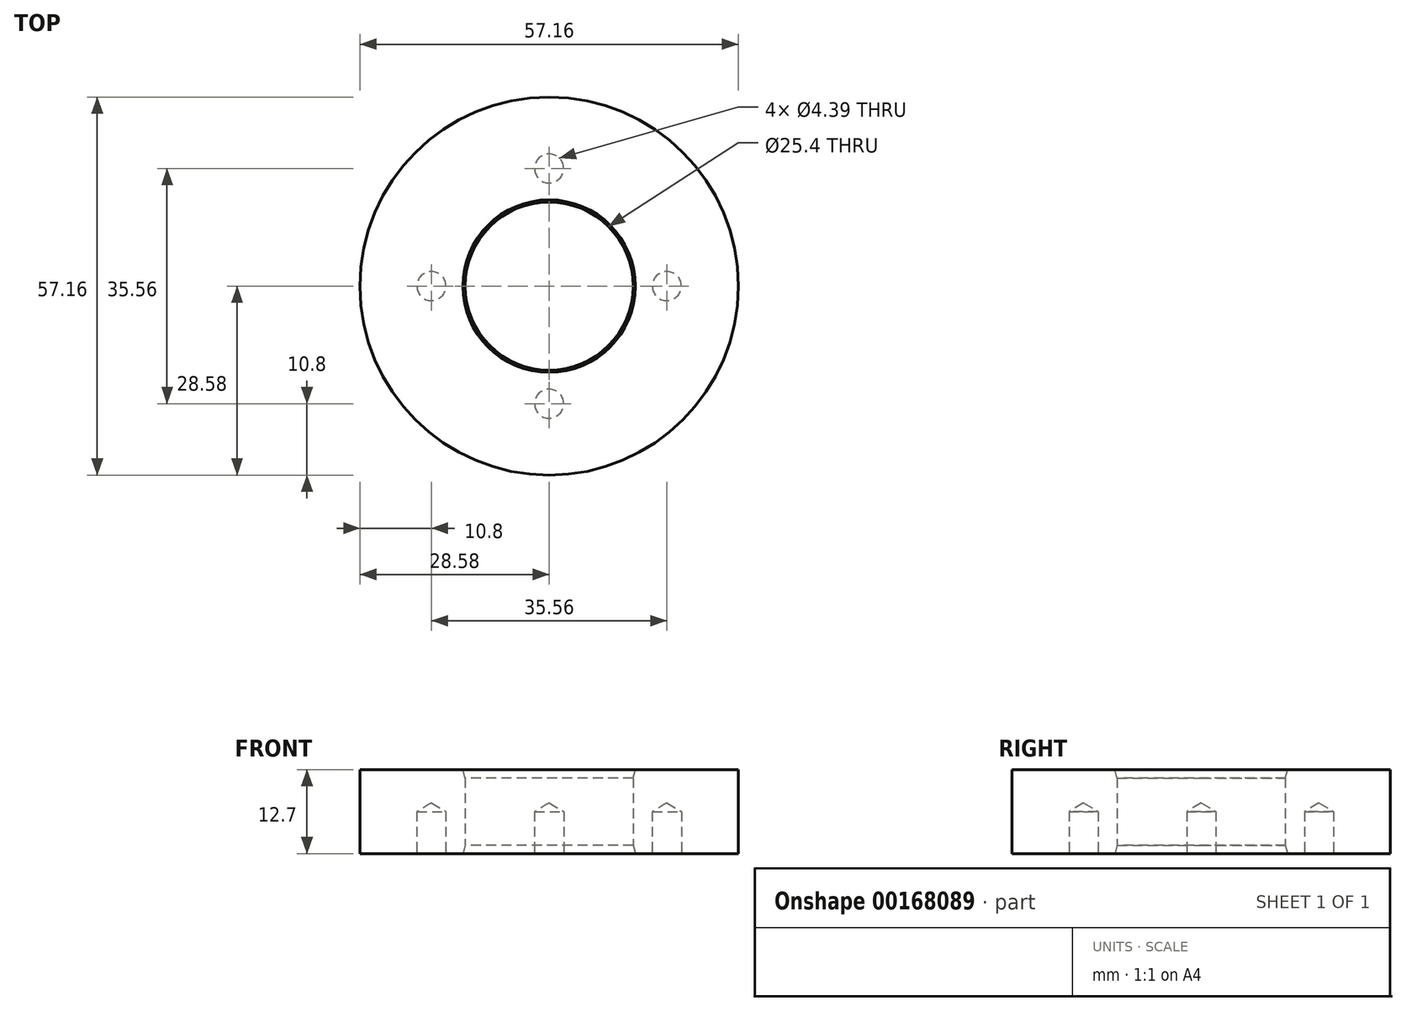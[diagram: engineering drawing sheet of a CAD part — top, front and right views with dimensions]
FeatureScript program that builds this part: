
annotation { "Feature Type Name" : "Feature", "Feature Type Description" : "" }
export const myFeature = defineFeature(function(context is Context, id is Id, definition is map)
    precondition{}
    {
        {
            var Q0;
            Q0=qCreatedBy(makeId("Top.planeOp"),FACE);
            var sketch = newSketch(context, id + "F0", { "sketchPlane" : qUnion([Q0])});
            skCircle(sketch, "E0", {"center": v(0, 0) * mm, "radius": 28.58 * mm});
            skCircle(sketch, "E1", {"center": v(0, 0) * mm, "radius": 12.7 * mm});
            skSolve(sketch);
        }
        {
            var Q0;
            Q0=qSketchRegion(id+"F0",true);
            extrude(context, id + "F1", {"entities" : qUnion([Q0]), "depth" : 12.7 * mm});
        }
        {
            var Q0;
            Q0=makeQuery(id+"F1.opExtrude","CAP_EDGE",EDGE,{"disambiguationData":[OSD([sQuery(id+"F0.wireOp",EDGE,"E1")])],"isStart":false});
            var Q1;
            Q1=makeQuery(id+"F1.opExtrude","CAP_EDGE",EDGE,{"disambiguationData":[OSD([sQuery(id+"F0.wireOp",EDGE,"E1")])],"isStart":true});
            chamfer(context, id + "F2", {"entities" : qUnion([Q0, Q1]), "chamferType" : ChamferType.OFFSET_ANGLE, "width" : 1.27 * mm, "oppositeDirection" : false, "angle" : 15 * degree, "tangentPropagation" : true});
        }
        {
            var Q0;
            Q0=makeQuery(id+"F1.opExtrude","CAP_FACE",FACE,{"disambiguationData":[OSD([sQuery(id+"F0.wireOp",EDGE,"E0"),sQuery(id+"F0.wireOp",EDGE,"E1")])],"isStart":true});
            var sketch = newSketch(context, id + "F3", { "sketchPlane" : qUnion([Q0])});
            skLineSegment(sketch, "E2", {"start": v(0, 0) * mm, "end": v(0, -12.7) * mm, "construction": true});
            skLineSegment(sketch, "E3", {"start": v(0, -12.7) * mm, "end": v(0, -22.86) * mm, "construction": true});
            skLineSegment(sketch, "E4", {"start": v(0, -22.86) * mm, "end": v(0, -12.7) * mm, "construction": true});
            skPoint(sketch, "E5", {"position": v(0, -17.78) * mm});
            skPoint(sketch, "E6.1.0", {"position": v(17.78, 0) * mm});
            skPoint(sketch, "E6.2.0", {"position": v(0, 17.78) * mm});
            skPoint(sketch, "E6.3.0", {"position": v(-17.78, 0) * mm});
            skPoint(sketch, "E6.center", {"position": v(0, 0) * mm});
            skSolve(sketch);
        }
        {
            var Q0;
            Q0=sQuery(id+"F3.wireOp",VERTEX,"E5");
            var Q1;
            Q1=sQuery(id+"F3.wireOp",VERTEX,"E6.3.0");
            var Q2;
            Q2=sQuery(id+"F3.wireOp",VERTEX,"E6.2.0");
            var Q3;
            Q3=sQuery(id+"F3.wireOp",VERTEX,"E6.1.0");
            var Q4;
            Q4=makeQuery(id+"F1.opExtrude","SWEPT_BODY",BODY,{"disambiguationData":[OSD([sQuery(id+"F0.wireOp",EDGE,"E0"),sQuery(id+"F0.wireOp",EDGE,"E1")])]});
            hole(context, id + "F4", {"style" : HoleStyle.SIMPLE, "endStyle" : HoleEndStyle.BLIND, "holeDiameter" : 4.4 * mm, "holeDepth" : 6.35 * mm, "locations" : qUnion([Q0, Q1, Q2, Q3]), "scope" : qUnion([Q4])});
        }
    });
